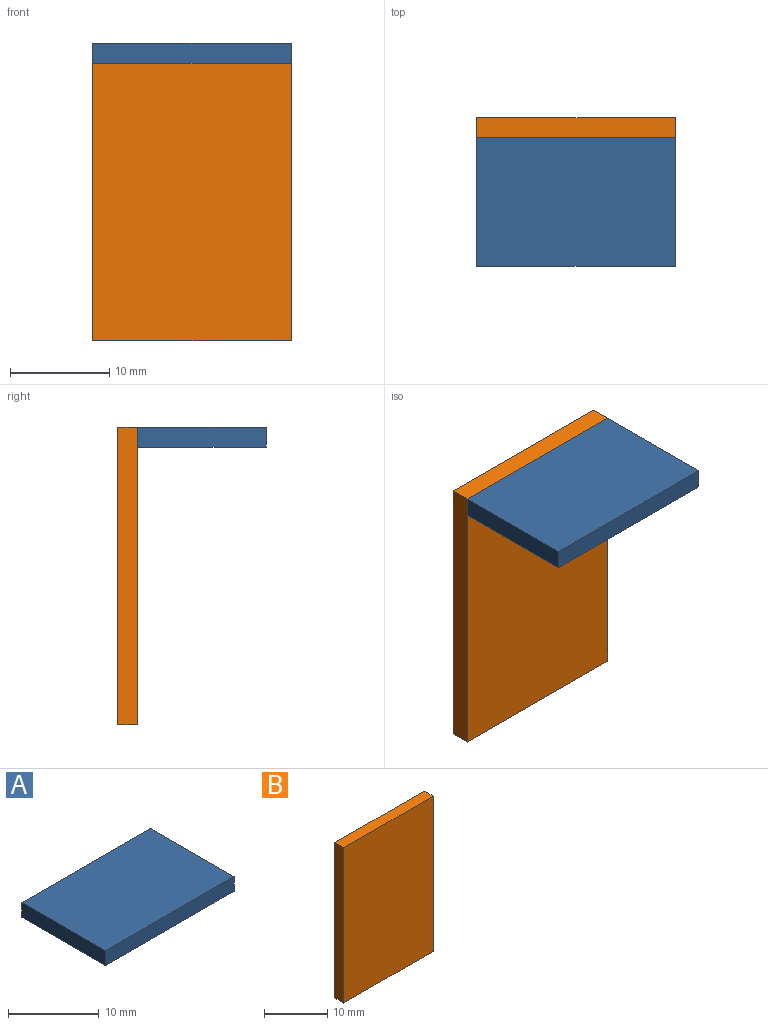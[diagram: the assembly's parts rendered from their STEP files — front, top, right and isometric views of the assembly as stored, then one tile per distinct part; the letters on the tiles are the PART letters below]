
ASSEMBLY  parts=2 mates=1
PART A: 6 faces, bbox 20x13x2 mm
  f0: plane 20x13mm, normal (0,0,1), area 260mm2, adj f1,f3,f4,f5
  f1: plane 20x2mm, normal (0,-1,0), area 40mm2, adj f0,f2,f4,f5
  f2: plane 20x13mm, normal (0,0,-1), area 260mm2, adj f1,f3,f4,f5
  f3: plane 20x2mm, normal (0,1,0), area 40mm2, adj f0,f2,f4,f5
  f4: plane 13x2mm, normal (1,0,0), area 26mm2, adj f0,f1,f2,f3
  f5: plane 13x2mm, normal (-1,0,0), area 26mm2, adj f0,f1,f2,f3
PART B: 6 faces, bbox 20x2x30 mm
  f0: plane 30x2mm, normal (-1,0,0), area 60mm2, adj f1,f3,f4,f5
  f1: plane 20x2mm, normal (0,0,-1), area 40mm2, adj f0,f2,f4,f5
  f2: plane 30x2mm, normal (1,0,0), area 60mm2, adj f1,f3,f4,f5
  f3: plane 20x2mm, normal (0,0,1), area 40mm2, adj f0,f2,f4,f5
  f4: plane 30x20mm, normal (0,-1,0), area 600mm2, adj f0,f1,f2,f3
  f5: plane 30x20mm, normal (0,1,0), area 600mm2, adj f0,f1,f2,f3
PLACE A t=(0,-5,0)mm
PLACE B t=(9.75,-39,2.59)mm
MATE fastened B.f4 <-> A.f3  axis (0,-1,0) through (10,-41,26.71)mm
